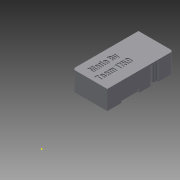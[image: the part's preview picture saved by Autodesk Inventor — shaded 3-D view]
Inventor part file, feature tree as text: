
AUTODESK INVENTOR PART (.ipt)
format: ipt  version: 2015 (Build 190159000, 159)  size: 570,368 bytes
history: native  units: in
note: dims shown in document units (in); Inventor stores cm internally (conversion verified against a paired STEP export)
features: extrude x10, sketch x9, projected_geometry x3, fillet x2, mirror x1
ambient origin geometry x8: Origin, YZ Plane, XZ Plane, XY Plane, X Axis, Y Axis, Z Axis, Center Point
bodies: Solid1 (feature_tree)
feature tree (25):
  extrude  "Extrusion1"  Depth=0.966in
  sketch  "Sketch2"  dims[d5=0.075in d6=0.1in d7=0.1in]
  fillet  "Fillet1"  Radius=0.533in
  fillet  "Fillet2"  Radius=0.075in
  extrude  "Extrusion2"  Depth=0.1in
  extrude  "Extrusion3"  Depth=0.125in
  extrude  "Extrusion4"  Depth=0.1in
  sketch  "Sketch6"  dims[d15=0.1in d16=0.1in]
  extrude  "Extrusion5"  Depth=0.1in
  sketch  "Sketch7"  dims[d17=0.1in d18=0.483in]
  extrude  "Extrusion7"  Depth=0.483in
  extrude  "Extrusion8"  Depth=0.1in
  extrude  "Extrusion9"  Depth=0.1in
  extrude  "Extrusion10"  Depth=0.5in
  mirror  "Mirror1"
  extrude  "Extrusion11"  Depth=0.45in
  sketch  "Sketch1"  dims[d0=1.833in d1=0.966in d2=0.533in d3=0.0in d4=0.075in]
  sketch  "Sketch4"  dims[d8=0.1in d9=0.1in d11=0.125in]
  sketch  "Sketch5"  dims[d13=0.175in d14=0.1in]
  sketch  "Sketch8"  dims[d19=0.0in d20=0.1in]
  projected_geometry  "Projected Loop1"
  sketch  "Sketch9"  dims[d21=0.24in d22=0.1in]
  projected_geometry  "Projected Loop2"
  sketch  "Sketch10"  dims[d23=0.545in d24=0.5in d25=0.45in d26=0.9in d27=0.533in d28=0.0in d29=0.279in d30=0.185in d32=0.3in d33=0.1in d34=0.533in d35=0.0in d36=0.1718in d37=1.2625in d38=0.025in d39=0.0in d40=0.05in d41=0.1in d42=0.025in d43=0.025in d46=0.05in d47=0.025in d48=0.0in d49=0.025in d50=0.0in d51=0.1in d52=0.5in d53=0.05in d54=0.0in d55=0.1in d56=0.0in d57=1.0in d58=0.5in d60=0.375in d61=0.025in d62=0.0in]
  projected_geometry  "Projected Loop3"
